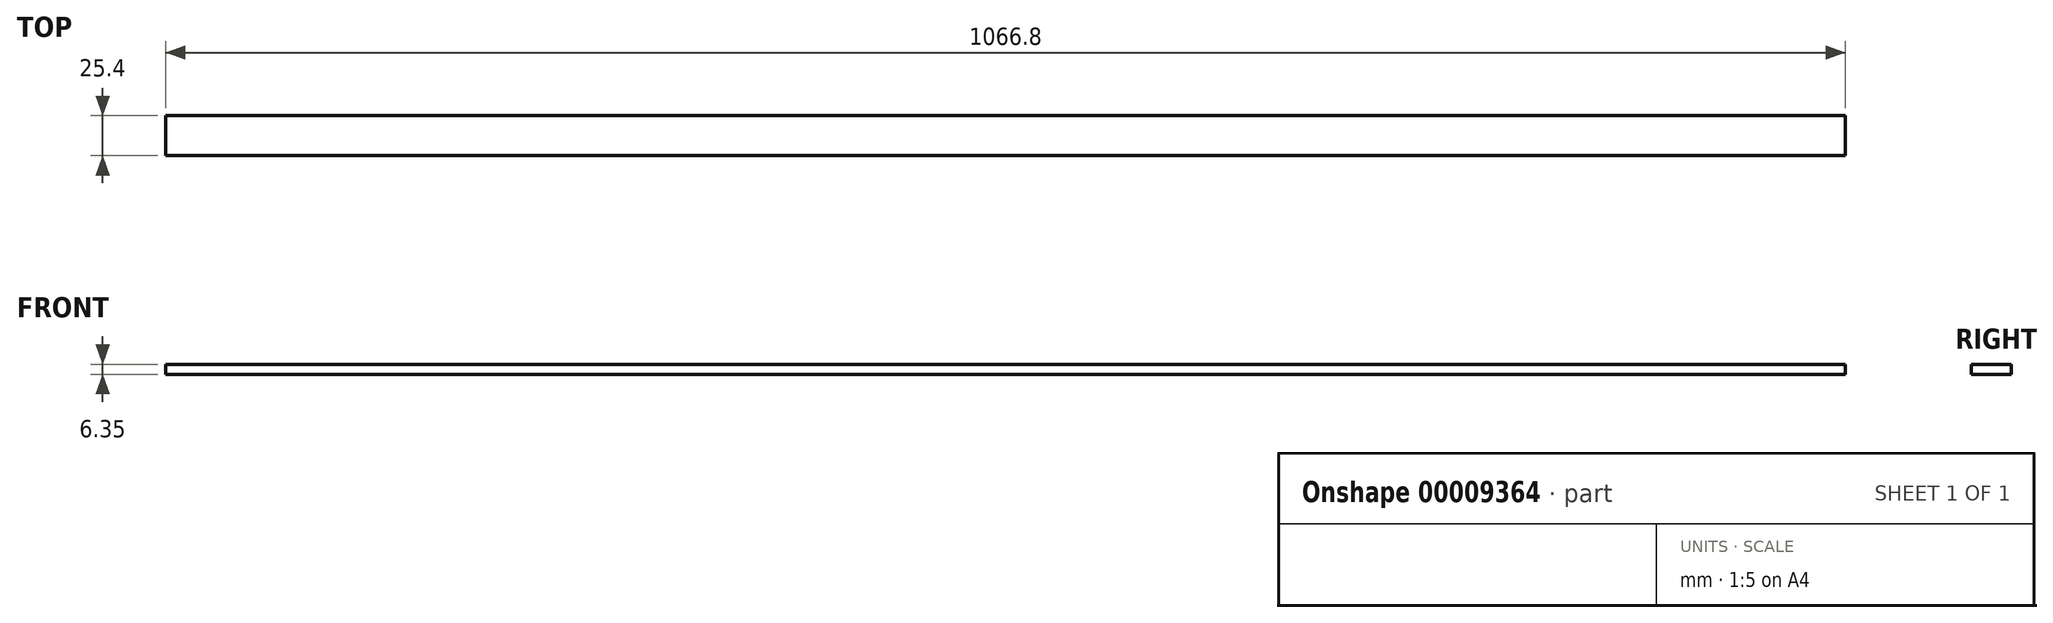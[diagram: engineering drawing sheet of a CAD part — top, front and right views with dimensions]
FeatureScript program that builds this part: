
annotation { "Feature Type Name" : "Feature", "Feature Type Description" : "" }
export const myFeature = defineFeature(function(context is Context, id is Id, definition is map)
    precondition{}
    {
        {
            var Q0;
            Q0=qCreatedBy(makeId("Front.planeOp"),FACE);
            var sketch = newSketch(context, id + "F0", { "sketchPlane" : qUnion([Q0])});
            skLineSegment(sketch, "E0.bottom", {"start": v(-12.84, 2.82) * mm, "end": v(12.56, 2.82) * mm});
            skLineSegment(sketch, "E0.top", {"start": v(-12.84, -3.53) * mm, "end": v(12.56, -3.53) * mm});
            skLineSegment(sketch, "E0.left", {"start": v(-12.84, 2.82) * mm, "end": v(-12.84, -3.53) * mm});
            skLineSegment(sketch, "E0.right", {"start": v(12.56, 2.82) * mm, "end": v(12.56, -3.53) * mm});
            skSolve(sketch);
        }
        {
            var Q0;
            Q0=makeQuery(id+"F0.imprint","IMPRINT",FACE,{"disambiguationData":[TD([[makeQuery(id+"F0.imprint","IMPRINT",EDGE,{"derivedFrom":sQuery(id+"F0.wireOp",EDGE,"E0.bottom")}),-1.0]])]});
            extrude(context, id + "F1", {"entities" : qUnion([Q0]), "depth" : 1066.8 * mm});
        }
        {
            var Q0;
            Q0=makeQuery(id+"F1.opExtrude","SWEPT_BODY",BODY,{"disambiguationData":[OSD([sQuery(id+"F0.wireOp",EDGE,"E0.bottom"),sQuery(id+"F0.wireOp",EDGE,"E0.top"),sQuery(id+"F0.wireOp",EDGE,"E0.left"),sQuery(id+"F0.wireOp",EDGE,"E0.right")])]});
            var Q1;
            Q1=makeQuery(id+"F1.opExtrude","CAP_EDGE",EDGE,{"disambiguationData":[OSD([sQuery(id+"F0.wireOp",EDGE,"E0.right")])],"isStart":true});
            transform(context, id + "F2", {"entities" : qUnion([Q0]), "transformType" : TransformType.ROTATION, "transformAxis" : qUnion([Q1]), "angle" : 90 * degree, "makeCopy" : false});
        }
    });
